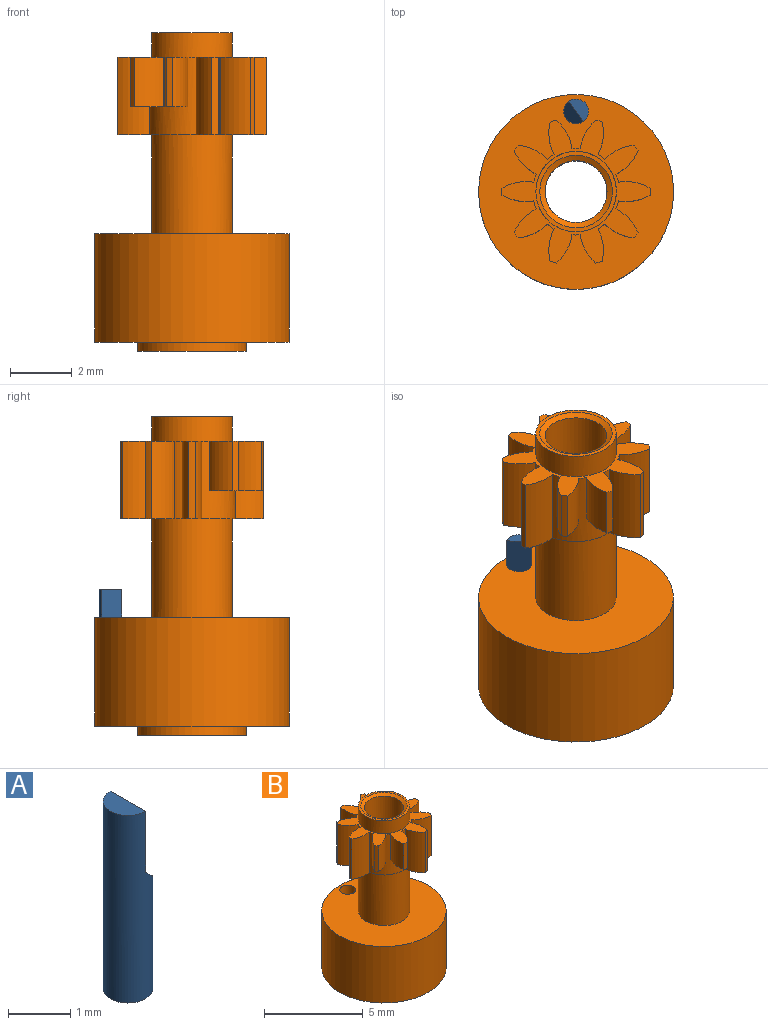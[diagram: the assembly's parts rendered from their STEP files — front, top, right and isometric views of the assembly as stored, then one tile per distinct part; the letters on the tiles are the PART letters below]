
ASSEMBLY  parts=2 mates=1
PART A: 5 faces, bbox 0.8x0.8x3.7 mm
  f0: cylinder r=0.4mm len=3.7mm, axis (0,0,-1), area 7.5mm2, adj f1,f2,f3,f4
  f1: plane 0.8x0.4mm, normal (0,0,1), area 0.3mm2, adj f0,f3
  f2: plane 0.8x0.8mm, normal (0,0,-1), area 0.5mm2, adj f0
  f3: plane 1.2x0.8mm, normal (1,0,0), area 1mm2, adj f0,f1,f4
  f4: plane 0.8x0.4mm, normal (0.71,0,0.71), area 0.4mm2, adj f0,f3
PART B: 54 faces, bbox 6.3x6.3x10.3 mm
  f0: plane 4.8x4.63mm, normal (0,0,-1), area 5.2mm2, adj f1,f8,f9,f10,f11,f12,f13,f14
  f1: cylinder r=1.5mm len=2.5mm, axis (0,0,-1), area 2.7mm2, adj f0,f8,f38,f39
  f2: cylinder r=1.5mm len=1.6mm, axis (0,0,-1), area 1.7mm2, adj f3,f8,f39,f40
  f3: cylinder r=2.4mm len=1.6mm, axis (0,0,-1), area 0.3mm2, adj f2,f4,f39,f40
  f4: cylinder r=1.5mm len=1.6mm, axis (0,0,-1), area 1.7mm2, adj f3,f8,f39,f40
  f5: cylinder r=1.5mm len=1.6mm, axis (0,0,-1), area 1.7mm2, adj f6,f8,f39,f41
  f6: cylinder r=2.4mm len=1.6mm, axis (0,0,-1), area 0.3mm2, adj f5,f7,f39,f41
  f7: cylinder r=1.5mm len=1.6mm, axis (0,0,-1), area 1.7mm2, adj f6,f8,f39,f41
  f8: cylinder r=1.4mm len=2.5mm, axis (0,0,-1), area 3.1mm2, adj f0,f1,f2,f4,f5,f7,f9,f39
  f9: cylinder r=1.5mm len=2.5mm, axis (0,0,-1), area 2.7mm2, adj f0,f8,f10,f39
  f10: cylinder r=2.4mm len=2.5mm, axis (0,0,-1), area 0.5mm2, adj f0,f9,f11,f39
  f11: cylinder r=1.5mm len=2.5mm, axis (0,0,-1), area 2.7mm2, adj f0,f10,f12,f39
  f12: cylinder r=1.4mm len=2.5mm, axis (0,0,-1), area 0.7mm2, adj f0,f11,f13,f39
  f13: cylinder r=1.5mm len=2.5mm, axis (0,0,-1), area 2.7mm2, adj f0,f12,f14,f39
  f14: cylinder r=2.4mm len=2.5mm, axis (0,0,-1), area 0.5mm2, adj f0,f13,f15,f39
  f15: cylinder r=1.5mm len=2.5mm, axis (0,0,-1), area 2.7mm2, adj f0,f14,f16,f39
  f16: cylinder r=1.4mm len=2.5mm, axis (0,0,-1), area 0.7mm2, adj f0,f15,f17,f39
  f17: cylinder r=1.5mm len=2.5mm, axis (0,0,-1), area 2.7mm2, adj f0,f16,f18,f39
  f18: cylinder r=2.4mm len=2.5mm, axis (0,0,-1), area 0.5mm2, adj f0,f17,f19,f39
  f19: cylinder r=1.5mm len=2.5mm, axis (0,0,-1), area 2.7mm2, adj f0,f18,f20,f39
  f20: cylinder r=1.4mm len=2.5mm, axis (0,0,-1), area 0.7mm2, adj f0,f19,f21,f39
  f21: cylinder r=1.5mm len=2.5mm, axis (0,0,-1), area 2.7mm2, adj f0,f20,f22,f39
  f22: cylinder r=2.4mm len=2.5mm, axis (0,0,-1), area 0.5mm2, adj f0,f21,f23,f39
  f23: cylinder r=1.5mm len=2.5mm, axis (0,0,-1), area 2.7mm2, adj f0,f22,f24,f39
  f24: cylinder r=1.4mm len=2.5mm, axis (0,0,-1), area 0.7mm2, adj f0,f23,f25,f39
  f25: cylinder r=1.5mm len=2.5mm, axis (0,0,-1), area 2.7mm2, adj f0,f24,f26,f39
  f26: cylinder r=2.4mm len=2.5mm, axis (0,0,-1), area 0.5mm2, adj f0,f25,f27,f39
  f27: cylinder r=1.5mm len=2.5mm, axis (0,0,-1), area 2.7mm2, adj f0,f26,f28,f39
  f28: cylinder r=1.4mm len=2.5mm, axis (0,0,-1), area 0.7mm2, adj f0,f27,f29,f39
  f29: cylinder r=1.5mm len=2.5mm, axis (0,0,-1), area 2.7mm2, adj f0,f28,f30,f39
  f30: cylinder r=2.4mm len=2.5mm, axis (0,0,-1), area 0.5mm2, adj f0,f29,f31,f39
  f31: cylinder r=1.5mm len=2.5mm, axis (0,0,-1), area 2.7mm2, adj f0,f30,f32,f39
  f32: cylinder r=1.4mm len=2.5mm, axis (0,0,-1), area 0.7mm2, adj f0,f31,f33,f39
  f33: cylinder r=1.5mm len=2.5mm, axis (0,0,-1), area 2.7mm2, adj f0,f32,f34,f39
  f34: cylinder r=2.4mm len=2.5mm, axis (0,0,-1), area 0.5mm2, adj f0,f33,f35,f39
  f35: cylinder r=1.5mm len=2.5mm, axis (0,0,-1), area 2.7mm2, adj f0,f34,f36,f39
  f36: cylinder r=1.4mm len=2.5mm, axis (0,0,-1), area 0.7mm2, adj f0,f35,f37,f39
  f37: cylinder r=1.5mm len=2.5mm, axis (0,0,-1), area 2.7mm2, adj f0,f36,f38,f39
  f38: cylinder r=2.4mm len=2.5mm, axis (0,0,-1), area 0.5mm2, adj f0,f1,f37,f39
  f39: plane 4.8x4.63mm, normal (0,0,1), area 6.3mm2, adj f1,f2,f3,f4,f5,f6,f7,f8
  f40: plane 1.07x0.94mm, normal (0,0,-1), area 0.5mm2, adj f2,f3,f4,f8
  f41: plane 1.11x0.75mm, normal (0,0,-1), area 0.5mm2, adj f5,f6,f7,f8
  f42: cylinder r=1.3mm len=3.2mm, axis (0,0,-1), area 26.1mm2, adj f0,f49
  f43: cylinder r=1mm len=9.51mm, axis (0,0,-1), area 59.7mm2, adj f44,f53
  f44: cone r=1mm half-angle=30deg, axis (0,0,-1), area 6mm2, adj f43,f45
  f45: plane 3.5x3.5mm, normal (0,0,-1), area 3.5mm2, adj f44,f46
  f46: cylinder r=1.75mm len=3.5mm, axis (0,0,-1), area 3.3mm2, adj f45,f47
  f47: plane 6.3x6.3mm, normal (0,0,-1), area 21mm2, adj f46,f48,f52
  f48: cylinder r=3.15mm len=6.3mm, axis (0,0,-1), area 69.3mm2, adj f47,f49
  f49: plane 6.3x6.3mm, normal (0,0,1), area 25.4mm2, adj f42,f48,f52
  f50: cylinder r=1.3mm len=2.6mm, axis (0,0,-1), area 6.5mm2, adj f39,f51
  f51: plane 2.6x2.6mm, normal (0,0,1), area 1mm2, adj f50,f53
  f52: cylinder r=0.4mm len=3.5mm, axis (0,0,1), area 8.8mm2, adj f47,f49
  f53: cone r=1.17mm half-angle=60deg, axis (0,0,1), area 1.4mm2, adj f43,f51
PLACE A rot(axis=(0,0,-1),144deg) t=(0,2.6,1)mm
PLACE B at identity
MATE fastened A.f0 <-> B.f52  axis (0,0,-1) through (0,2.6,4.7)mm
